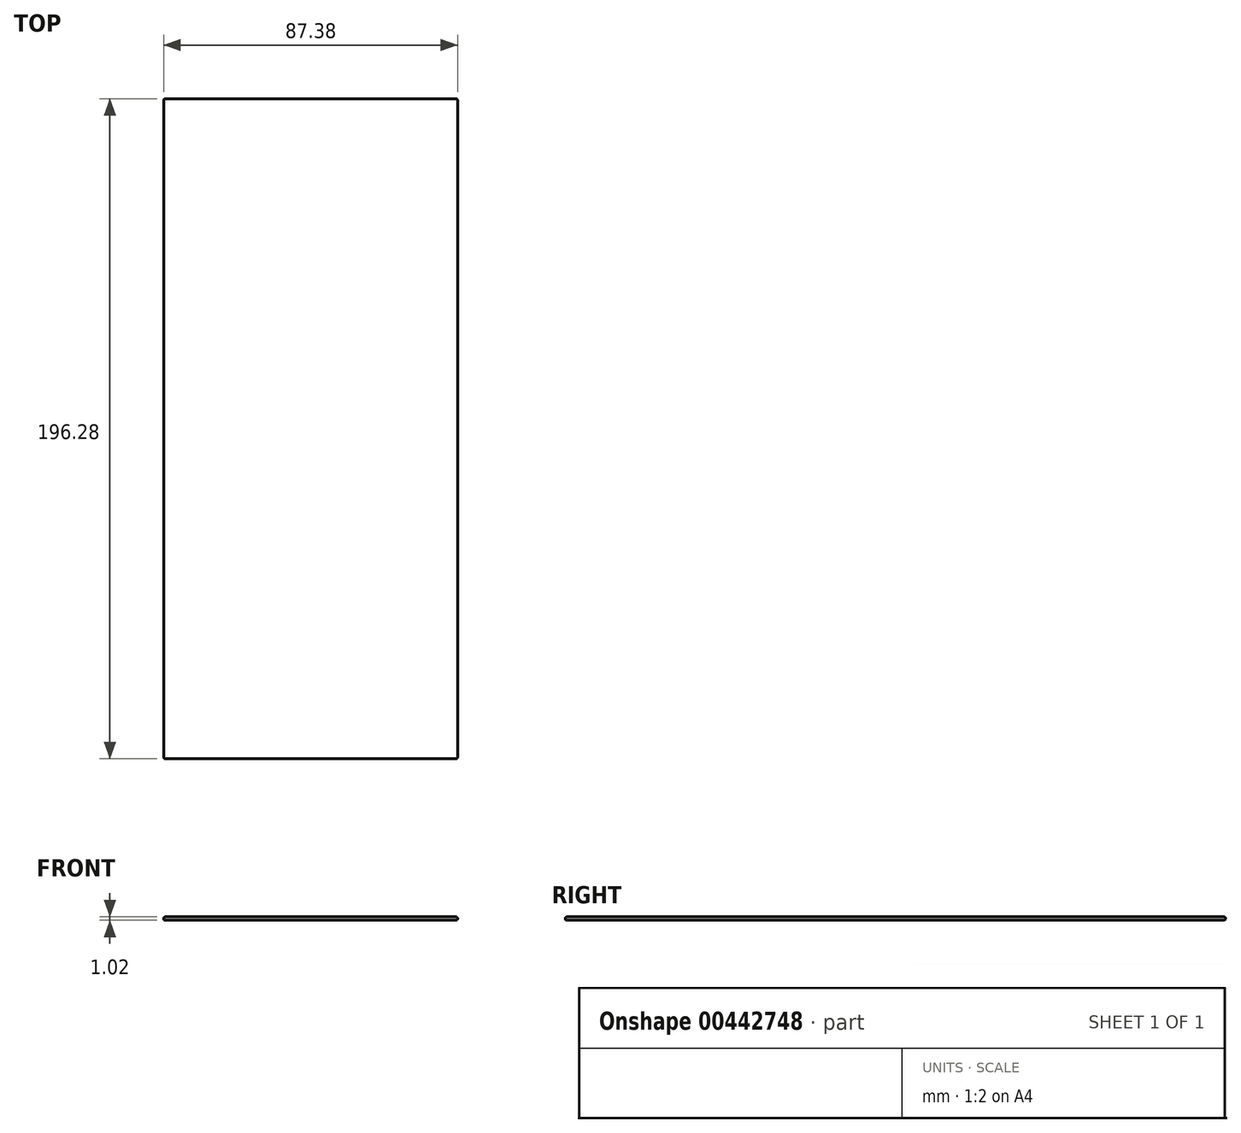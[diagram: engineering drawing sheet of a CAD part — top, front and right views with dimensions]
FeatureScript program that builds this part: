
annotation { "Feature Type Name" : "Feature", "Feature Type Description" : "" }
export const myFeature = defineFeature(function(context is Context, id is Id, definition is map)
    precondition{}
    {
        {
            var Q0;
            Q0=qCreatedBy(makeId("Top.planeOp"),FACE);
            var sketch = newSketch(context, id + "F0", { "sketchPlane" : qUnion([Q0])});
            skLineSegment(sketch, "E0.bottom", {"start": v(43.69, -98.14) * mm, "end": v(-43.69, -98.14) * mm});
            skLineSegment(sketch, "E0.top", {"start": v(43.69, 98.14) * mm, "end": v(-43.69, 98.14) * mm});
            skLineSegment(sketch, "E0.left", {"start": v(43.69, -98.14) * mm, "end": v(43.69, 98.14) * mm});
            skLineSegment(sketch, "E0.right", {"start": v(-43.69, -98.14) * mm, "end": v(-43.69, 98.14) * mm});
            skPoint(sketch, "E0.middle", {"position": v(0, 0) * mm});
            skSolve(sketch);
        }
        {
            var Q0;
            Q0 = qSketchRegion(id + "F0", true);
            extrude(context, id + "F1", {"entities" : qUnion([Q0]), "depth" : 1.02 * mm, "offsetDistance" : 25.4 * mm});
        }
        {
            var Q0;
            Q0=makeQuery(id+"F1.opExtrude","SWEPT_FACE",FACE,{"disambiguationData":[OSD([sQuery(id+"F0.wireOp",EDGE,"E0.top")])]});
            var Q1;
            Q1=makeQuery(id+"F1.opExtrude","SWEPT_FACE",FACE,{"disambiguationData":[OSD([sQuery(id+"F0.wireOp",EDGE,"E0.right")])]});
            var Q2;
            Q2=makeQuery(id+"F1.opExtrude","SWEPT_FACE",FACE,{"disambiguationData":[OSD([sQuery(id+"F0.wireOp",EDGE,"E0.bottom")])]});
            var Q3;
            Q3=makeQuery(id+"F1.opExtrude","SWEPT_FACE",FACE,{"disambiguationData":[OSD([sQuery(id+"F0.wireOp",EDGE,"E0.left")])]});
            fillet(context, id + "F2", {"entities" : qUnion([Q0, Q1, Q2, Q3]), "radius" : 0.5 * mm, "tangentPropagation" : true, "allowEdgeOverflow" : false});
        }
    });
